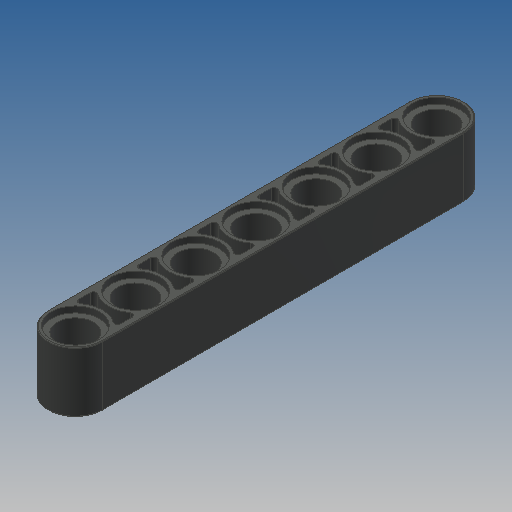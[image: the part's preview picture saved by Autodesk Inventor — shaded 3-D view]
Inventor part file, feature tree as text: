
AUTODESK INVENTOR PART (.ipt)
format: ipt  version: 2022.2 (Build 262287000, 287)  size: 358,912 bytes
history: native  units: mm
features: extrude x3, sketch x2, mirror x1, fillet x1
ambient origin geometry x8: Origin, YZ Plane, XZ Plane, XY Plane, X Axis, Y Axis, Z Axis, Center Point
bodies: Solid1 (feature_tree)
feature tree (7):
  extrude  "Extrusion1"  Depth=7.2mm
  sketch  "Sketch6"  dims[d41=0.8mm d42=0.0mm d43=3.1mm d44=0.0mm d48=48.0mm d49=6.4mm d50=4.8mm d51=8.0mm d52=0.8mm d53=60.0mm d55=8.0mm d56=10.0mm d58=10.0mm d60=0.4mm d61=0.1mm]
  extrude  "Extrusion7"  Depth=3.1mm TaperAngle=0.0deg
  extrude  "Extrusion8"  Depth=0.1mm
  mirror  "Mirror1"
  fillet  "Fillet2"  Radius=6.4mm
  sketch  "Sketch1"  dims[d14=8.0mm d15=0.0mm d32=7.2mm]
